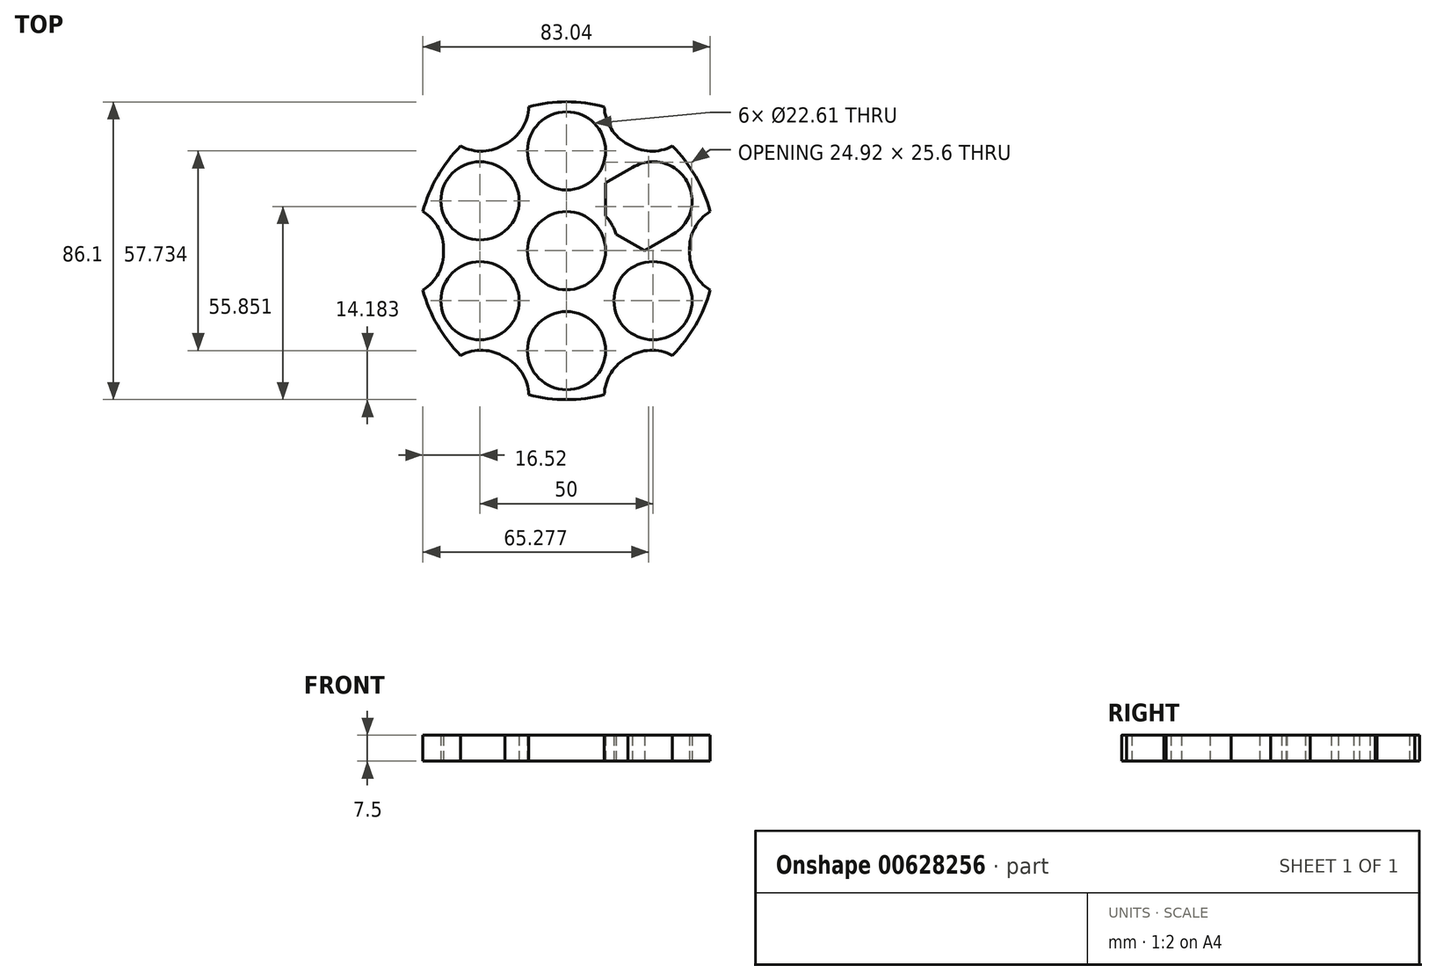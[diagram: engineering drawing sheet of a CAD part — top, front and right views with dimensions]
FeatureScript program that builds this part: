
annotation { "Feature Type Name" : "Feature", "Feature Type Description" : "" }
export const myFeature = defineFeature(function(context is Context, id is Id, definition is map)
    precondition{}
    {
        {
            var Q0;
            Q0=qCreatedBy(makeId("Top.planeOp"),FACE);
            var sketch = newSketch(context, id + "F0", { "sketchPlane" : qUnion([Q0])});
            skCircle(sketch, "E0", {"center": v(0, 0) * mm, "radius": 11.3 * mm});
            skCircle(sketch, "E1", {"center": v(0, 0) * mm, "radius": 15.11 * mm});
            skCircle(sketch, "E2", {"center": v(0, 0) * mm, "radius": 43.05 * mm});
            skCircle(sketch, "E3", {"center": v(0, 28.87) * mm, "radius": 11.3 * mm});
            skLineSegment(sketch, "E4", {"start": v(11.3, 29.23) * mm, "end": v(11.3, 10.04) * mm});
            skLineSegment(sketch, "E5", {"start": v(11.3, 10.04) * mm, "end": v(11.3, 29.23) * mm});
            skLineSegment(sketch, "E6", {"start": v(11.3, 29.23) * mm, "end": v(10.9, 41.65) * mm});
            skPoint(sketch, "E7.endSnap0", {"position": v(11.1, 35.44) * mm});
            skLineSegment(sketch, "E8.MirrorCS", {"start": v(-11.3, 29.23) * mm, "end": v(-11.3, 10.04) * mm});
            skLineSegment(sketch, "E9.MirrorCS", {"start": v(-11.3, 29.23) * mm, "end": v(-10.9, 41.65) * mm});
            skPoint(sketch, "E10.MirrorCS.end.orphan", {"position": v(-24.45, 35.44) * mm});
            skPoint(sketch, "E10.MirrorCS.start.orphan", {"position": v(-10.9, 41.65) * mm});
            skPoint(sketch, "E7.end.orphan", {"position": v(24.45, 35.44) * mm});
            skPoint(sketch, "E11.end.orphan", {"position": v(32.4, 28.36) * mm});
            skPoint(sketch, "E12.MirrorCS.end.orphan", {"position": v(-32.4, 28.36) * mm});
            skArc(sketch, "E13", {"start": v(10.9, 41.65) * mm, "mid": v(17.36, 31.03) * mm, "end": v(29.78, 31.09) * mm});
            skArc(sketch, "E14.MirrorCS", {"start": v(-10.9, 41.65) * mm, "mid": v(-17.36, 31.03) * mm, "end": v(-29.78, 31.09) * mm});
            skLineSegment(sketch, "E15.1.0", {"start": v(-30.96, 4.83) * mm, "end": v(-41.52, 11.39) * mm});
            skArc(sketch, "E15.1.1", {"start": v(-41.52, 11.39) * mm, "mid": v(-35.55, 0.49) * mm, "end": v(-41.82, -10.25) * mm});
            skLineSegment(sketch, "E15.1.2", {"start": v(-3.05, 14.8) * mm, "end": v(-19.66, 24.4) * mm});
            skLineSegment(sketch, "E15.1.3", {"start": v(-30.96, 4.83) * mm, "end": v(-14.34, -4.76) * mm});
            skCircle(sketch, "E15.1.4", {"center": v(-25, 14.43) * mm, "radius": 11.3 * mm});
            skLineSegment(sketch, "E15.1.5", {"start": v(-19.66, 24.4) * mm, "end": v(-30.62, 30.26) * mm});
            skArc(sketch, "E15.1.6", {"start": v(-30.62, 30.26) * mm, "mid": v(-18.2, 30.55) * mm, "end": v(-12.03, 41.34) * mm});
            skLineSegment(sketch, "E15.2.0", {"start": v(-19.66, -24.4) * mm, "end": v(-30.62, -30.26) * mm});
            skArc(sketch, "E15.2.1", {"start": v(-30.62, -30.26) * mm, "mid": v(-18.2, -30.55) * mm, "end": v(-12.03, -41.34) * mm});
            skLineSegment(sketch, "E15.2.2", {"start": v(-14.34, 4.76) * mm, "end": v(-30.96, -4.83) * mm});
            skLineSegment(sketch, "E15.2.3", {"start": v(-19.66, -24.4) * mm, "end": v(-3.05, -14.8) * mm});
            skCircle(sketch, "E15.2.4", {"center": v(-25, -14.43) * mm, "radius": 11.3 * mm});
            skLineSegment(sketch, "E15.2.5", {"start": v(-30.96, -4.83) * mm, "end": v(-41.52, -11.39) * mm});
            skArc(sketch, "E15.2.6", {"start": v(-41.52, -11.39) * mm, "mid": v(-35.55, -0.49) * mm, "end": v(-41.82, 10.25) * mm});
            skLineSegment(sketch, "E15.3.0", {"start": v(11.3, -29.23) * mm, "end": v(10.9, -41.65) * mm});
            skArc(sketch, "E15.3.1", {"start": v(10.9, -41.65) * mm, "mid": v(17.36, -31.03) * mm, "end": v(29.78, -31.09) * mm});
            skLineSegment(sketch, "E15.3.2", {"start": v(-11.3, -10.04) * mm, "end": v(-11.3, -29.23) * mm});
            skLineSegment(sketch, "E15.3.3", {"start": v(11.3, -29.23) * mm, "end": v(11.3, -10.04) * mm});
            skCircle(sketch, "E15.3.4", {"center": v(0, -28.87) * mm, "radius": 11.3 * mm});
            skLineSegment(sketch, "E15.3.5", {"start": v(-11.3, -29.23) * mm, "end": v(-10.9, -41.65) * mm});
            skArc(sketch, "E15.3.6", {"start": v(-10.9, -41.65) * mm, "mid": v(-17.36, -31.03) * mm, "end": v(-29.78, -31.09) * mm});
            skLineSegment(sketch, "E15.4.0", {"start": v(30.96, -4.83) * mm, "end": v(41.52, -11.39) * mm});
            skArc(sketch, "E15.4.1", {"start": v(41.52, -11.39) * mm, "mid": v(35.55, -0.49) * mm, "end": v(41.82, 10.25) * mm});
            skLineSegment(sketch, "E15.4.2", {"start": v(3.05, -14.8) * mm, "end": v(19.66, -24.4) * mm});
            skLineSegment(sketch, "E15.4.3", {"start": v(30.96, -4.83) * mm, "end": v(14.34, 4.76) * mm});
            skCircle(sketch, "E15.4.4", {"center": v(25, -14.43) * mm, "radius": 11.3 * mm});
            skLineSegment(sketch, "E15.4.5", {"start": v(19.66, -24.4) * mm, "end": v(30.62, -30.26) * mm});
            skArc(sketch, "E15.4.6", {"start": v(30.62, -30.26) * mm, "mid": v(18.2, -30.55) * mm, "end": v(12.03, -41.34) * mm});
            skLineSegment(sketch, "E15.5.0", {"start": v(19.66, 24.4) * mm, "end": v(30.62, 30.26) * mm});
            skArc(sketch, "E15.5.1", {"start": v(30.62, 30.26) * mm, "mid": v(18.2, 30.55) * mm, "end": v(12.03, 41.34) * mm});
            skLineSegment(sketch, "E15.5.2", {"start": v(14.34, -4.76) * mm, "end": v(30.96, 4.83) * mm});
            skLineSegment(sketch, "E15.5.3", {"start": v(19.66, 24.4) * mm, "end": v(3.05, 14.8) * mm});
            skCircle(sketch, "E15.5.4", {"center": v(25, 14.43) * mm, "radius": 11.3 * mm});
            skLineSegment(sketch, "E15.5.5", {"start": v(30.96, 4.83) * mm, "end": v(41.52, 11.39) * mm});
            skArc(sketch, "E15.5.6", {"start": v(41.52, 11.39) * mm, "mid": v(35.55, 0.49) * mm, "end": v(41.82, -10.25) * mm});
            skPoint(sketch, "E16.orphan", {"position": v(0, 63.52) * mm});
            skLineSegment(sketch, "E17.trimOffspring", {"start": v(0, 11.3) * mm, "end": v(0, -11.3) * mm});
            skSolve(sketch);
        }
        {
            var Q0;
            {var subQ0=sQuery(id+"F0.wireOp",EDGE,"E15.3.0");Q0=makeQuery(id+"F0.imprint","IMPRINT",FACE,{"disambiguationData":[TD([[makeQuery(id+"F0.imprint","IMPRINT",EDGE,{"derivedFrom":subQ0}),-1.0]])]});}
            var Q1;
            {var subQ5=sQuery(id+"F0.wireOp",EDGE,"E15.2.3");var subQ6=sQuery(id+"F0.wireOp",EDGE,"E1");var subQ7=makeQuery(id+"F0.imprint","INTERSECT",VERTEX,{"derivedFrom":[subQ6,subQ5]});Q1=makeQuery(id+"F0.imprint","IMPRINT",FACE,{"disambiguationData":[TD([[makeQuery(id+"F0.imprint","IMPRINT",EDGE,{"disambiguationData":[TD([[subQ7,-1.0]])],"derivedFrom":subQ6}),-1.0]])]});}
            var Q2;
            {var subQ7=sQuery(id+"F0.wireOp",EDGE,"E15.2.0");Q2=makeQuery(id+"F0.imprint","IMPRINT",FACE,{"disambiguationData":[TD([[makeQuery(id+"F0.imprint","IMPRINT",EDGE,{"derivedFrom":subQ7}),1.0]])]});}
            var Q3;
            {var subQ0=sQuery(id+"F0.wireOp",EDGE,"E15.2.3");var subQ1=sQuery(id+"F0.wireOp",EDGE,"E1");var subQ2=makeQuery(id+"F0.imprint","INTERSECT",VERTEX,{"derivedFrom":[subQ1,subQ0]});Q3=makeQuery(id+"F0.imprint","IMPRINT",FACE,{"disambiguationData":[TD([[makeQuery(id+"F0.imprint","IMPRINT",EDGE,{"disambiguationData":[TD([[subQ2,1.0]])],"derivedFrom":subQ1}),-1.0]])]});}
            var Q4;
            {var subQ0=sQuery(id+"F0.wireOp",EDGE,"E15.3.3");var subQ1=sQuery(id+"F0.wireOp",EDGE,"E1");var subQ2=makeQuery(id+"F0.imprint","INTERSECT",VERTEX,{"derivedFrom":[subQ1,subQ0]});Q4=makeQuery(id+"F0.imprint","IMPRINT",FACE,{"disambiguationData":[TD([[makeQuery(id+"F0.imprint","IMPRINT",EDGE,{"disambiguationData":[TD([[subQ2,1.0]])],"derivedFrom":subQ1}),-1.0]])]});}
            var Q5;
            {var subQ8=sQuery(id+"F0.wireOp",EDGE,"E17.trimOffspring");var subQ9=sQuery(id+"F0.wireOp",EDGE,"E0");var subQ10=makeQuery(id+"F0.imprint","INTERSECT",VERTEX,{"disambiguationData":[OD(0.0)],"derivedFrom":[subQ9,subQ8]});Q5=makeQuery(id+"F0.imprint","IMPRINT",FACE,{"disambiguationData":[TD([[makeQuery(id+"F0.imprint","IMPRINT",EDGE,{"disambiguationData":[TD([[subQ10,-1.0]])],"derivedFrom":subQ9}),-1.0]])]});}
            var Q6;
            {var subQ1=sQuery(id+"F0.wireOp",EDGE,"E15.1.3");var subQ5=sQuery(id+"F0.wireOp",EDGE,"E1");var subQ6=makeQuery(id+"F0.imprint","INTERSECT",VERTEX,{"derivedFrom":[subQ5,subQ1]});Q6=makeQuery(id+"F0.imprint","IMPRINT",FACE,{"disambiguationData":[TD([[makeQuery(id+"F0.imprint","IMPRINT",EDGE,{"disambiguationData":[TD([[subQ6,-1.0]])],"derivedFrom":subQ5}),-1.0]])]});}
            var Q7;
            {var subQ7=sQuery(id+"F0.wireOp",EDGE,"E15.3.0");Q7=makeQuery(id+"F0.imprint","IMPRINT",FACE,{"disambiguationData":[TD([[makeQuery(id+"F0.imprint","IMPRINT",EDGE,{"derivedFrom":subQ7}),1.0]])]});}
            var Q8;
            {var subQ1=sQuery(id+"F0.wireOp",EDGE,"E15.3.3");var subQ9=sQuery(id+"F0.wireOp",EDGE,"E1");var subQ10=makeQuery(id+"F0.imprint","INTERSECT",VERTEX,{"derivedFrom":[subQ9,subQ1]});Q8=makeQuery(id+"F0.imprint","IMPRINT",FACE,{"disambiguationData":[TD([[makeQuery(id+"F0.imprint","IMPRINT",EDGE,{"disambiguationData":[TD([[subQ10,-1.0]])],"derivedFrom":subQ9}),-1.0]])]});}
            var Q9;
            {var subQ0=sQuery(id+"F0.wireOp",EDGE,"E15.4.0");Q9=makeQuery(id+"F0.imprint","IMPRINT",FACE,{"disambiguationData":[TD([[makeQuery(id+"F0.imprint","IMPRINT",EDGE,{"derivedFrom":subQ0}),-1.0]])]});}
            var Q10;
            {var subQ0=sQuery(id+"F0.wireOp",EDGE,"E15.2.0");Q10=makeQuery(id+"F0.imprint","IMPRINT",FACE,{"disambiguationData":[TD([[makeQuery(id+"F0.imprint","IMPRINT",EDGE,{"derivedFrom":subQ0}),-1.0]])]});}
            var Q11;
            {var subQ7=sQuery(id+"F0.wireOp",EDGE,"E15.1.0");Q11=makeQuery(id+"F0.imprint","IMPRINT",FACE,{"disambiguationData":[TD([[makeQuery(id+"F0.imprint","IMPRINT",EDGE,{"derivedFrom":subQ7}),1.0]])]});}
            var Q12;
            {var subQ0=sQuery(id+"F0.wireOp",EDGE,"E15.1.3");var subQ1=sQuery(id+"F0.wireOp",EDGE,"E1");var subQ2=makeQuery(id+"F0.imprint","INTERSECT",VERTEX,{"derivedFrom":[subQ1,subQ0]});Q12=makeQuery(id+"F0.imprint","IMPRINT",FACE,{"disambiguationData":[TD([[makeQuery(id+"F0.imprint","IMPRINT",EDGE,{"disambiguationData":[TD([[subQ2,1.0]])],"derivedFrom":subQ1}),-1.0]])]});}
            var Q13;
            {var subQ1=sQuery(id+"F0.wireOp",EDGE,"E8.MirrorCS");var subQ5=sQuery(id+"F0.wireOp",EDGE,"E1");var subQ6=makeQuery(id+"F0.imprint","INTERSECT",VERTEX,{"derivedFrom":[subQ5,subQ1]});Q13=makeQuery(id+"F0.imprint","IMPRINT",FACE,{"disambiguationData":[TD([[makeQuery(id+"F0.imprint","IMPRINT",EDGE,{"disambiguationData":[TD([[subQ6,-1.0]])],"derivedFrom":subQ5}),-1.0]])]});}
            var Q14;
            {var subQ0=sQuery(id+"F0.wireOp",EDGE,"E15.1.0");Q14=makeQuery(id+"F0.imprint","IMPRINT",FACE,{"disambiguationData":[TD([[makeQuery(id+"F0.imprint","IMPRINT",EDGE,{"derivedFrom":subQ0}),-1.0]])]});}
            var Q15;
            {var subQ7=sQuery(id+"F0.wireOp",EDGE,"E15.4.0");Q15=makeQuery(id+"F0.imprint","IMPRINT",FACE,{"disambiguationData":[TD([[makeQuery(id+"F0.imprint","IMPRINT",EDGE,{"derivedFrom":subQ7}),1.0]])]});}
            var Q16;
            {var subQ0=sQuery(id+"F0.wireOp",EDGE,"E15.4.3");var subQ1=sQuery(id+"F0.wireOp",EDGE,"E1");var subQ2=makeQuery(id+"F0.imprint","INTERSECT",VERTEX,{"derivedFrom":[subQ1,subQ0]});Q16=makeQuery(id+"F0.imprint","IMPRINT",FACE,{"disambiguationData":[TD([[makeQuery(id+"F0.imprint","IMPRINT",EDGE,{"disambiguationData":[TD([[subQ2,1.0]])],"derivedFrom":subQ1}),-1.0]])]});}
            var Q17;
            {var subQ1=sQuery(id+"F0.wireOp",EDGE,"E1");var subQ7=sQuery(id+"F0.wireOp",EDGE,"E5");var subQ8=makeQuery(id+"F0.imprint","INTERSECT",VERTEX,{"derivedFrom":[subQ1,subQ7]});Q17=makeQuery(id+"F0.imprint","IMPRINT",FACE,{"disambiguationData":[TD([[makeQuery(id+"F0.imprint","IMPRINT",EDGE,{"disambiguationData":[TD([[subQ8,1.0]])],"derivedFrom":subQ1}),-1.0]])]});}
            var Q18;
            {var subQ0=sQuery(id+"F0.wireOp",EDGE,"E15.5.0");Q18=makeQuery(id+"F0.imprint","IMPRINT",FACE,{"disambiguationData":[TD([[makeQuery(id+"F0.imprint","IMPRINT",EDGE,{"derivedFrom":subQ0}),-1.0]])]});}
            var Q19;
            {var subQ0=sQuery(id+"F0.wireOp",EDGE,"E5");var subQ1=sQuery(id+"F0.wireOp",EDGE,"E1");var subQ2=makeQuery(id+"F0.imprint","INTERSECT",VERTEX,{"derivedFrom":[subQ1,subQ0]});Q19=makeQuery(id+"F0.imprint","IMPRINT",FACE,{"disambiguationData":[TD([[makeQuery(id+"F0.imprint","IMPRINT",EDGE,{"disambiguationData":[TD([[subQ2,-1.0]])],"derivedFrom":subQ1}),-1.0]])]});}
            var Q20;
            {var subQ0=sQuery(id+"F0.wireOp",EDGE,"E8.MirrorCS");var subQ1=sQuery(id+"F0.wireOp",EDGE,"E1");var subQ2=makeQuery(id+"F0.imprint","INTERSECT",VERTEX,{"derivedFrom":[subQ1,subQ0]});Q20=makeQuery(id+"F0.imprint","IMPRINT",FACE,{"disambiguationData":[TD([[makeQuery(id+"F0.imprint","IMPRINT",EDGE,{"disambiguationData":[TD([[subQ2,1.0]])],"derivedFrom":subQ1}),-1.0]])]});}
            var Q21;
            {var subQ3=sQuery(id+"F0.wireOp",EDGE,"E15.1.2");var subQ9=sQuery(id+"F0.wireOp",EDGE,"E1");var subQ10=makeQuery(id+"F0.imprint","INTERSECT",VERTEX,{"derivedFrom":[subQ9,subQ3]});Q21=makeQuery(id+"F0.imprint","IMPRINT",FACE,{"disambiguationData":[TD([[makeQuery(id+"F0.imprint","IMPRINT",EDGE,{"disambiguationData":[TD([[subQ10,1.0]])],"derivedFrom":subQ9}),-1.0]])]});}
            var Q22;
            {var subQ0=sQuery(id+"F0.wireOp",EDGE,"E6");Q22=makeQuery(id+"F0.imprint","IMPRINT",FACE,{"disambiguationData":[TD([[makeQuery(id+"F0.imprint","IMPRINT",EDGE,{"derivedFrom":subQ0}),1.0]])]});}
            var Q23;
            {var subQ1=sQuery(id+"F0.wireOp",EDGE,"E9.MirrorCS");Q23=makeQuery(id+"F0.imprint","IMPRINT",FACE,{"disambiguationData":[TD([[makeQuery(id+"F0.imprint","IMPRINT",EDGE,{"derivedFrom":subQ1}),1.0]])]});}
            var Q24;
            {var subQ1=sQuery(id+"F0.wireOp",EDGE,"E6");Q24=makeQuery(id+"F0.imprint","IMPRINT",FACE,{"disambiguationData":[TD([[makeQuery(id+"F0.imprint","IMPRINT",EDGE,{"derivedFrom":subQ1}),-1.0]])]});}
            extrude(context, id + "F1", {"entities" : qUnion([Q0, Q1, Q2, Q3, Q4, Q5, Q6, Q7, Q8, Q9, Q10, Q11, Q12, Q13, Q14, Q15, Q16, Q17, Q18, Q19, Q20, Q21, Q22, Q23, Q24]), "depth" : 7.5 * mm, "offsetDistance" : 25.4 * mm});
        }
    });
